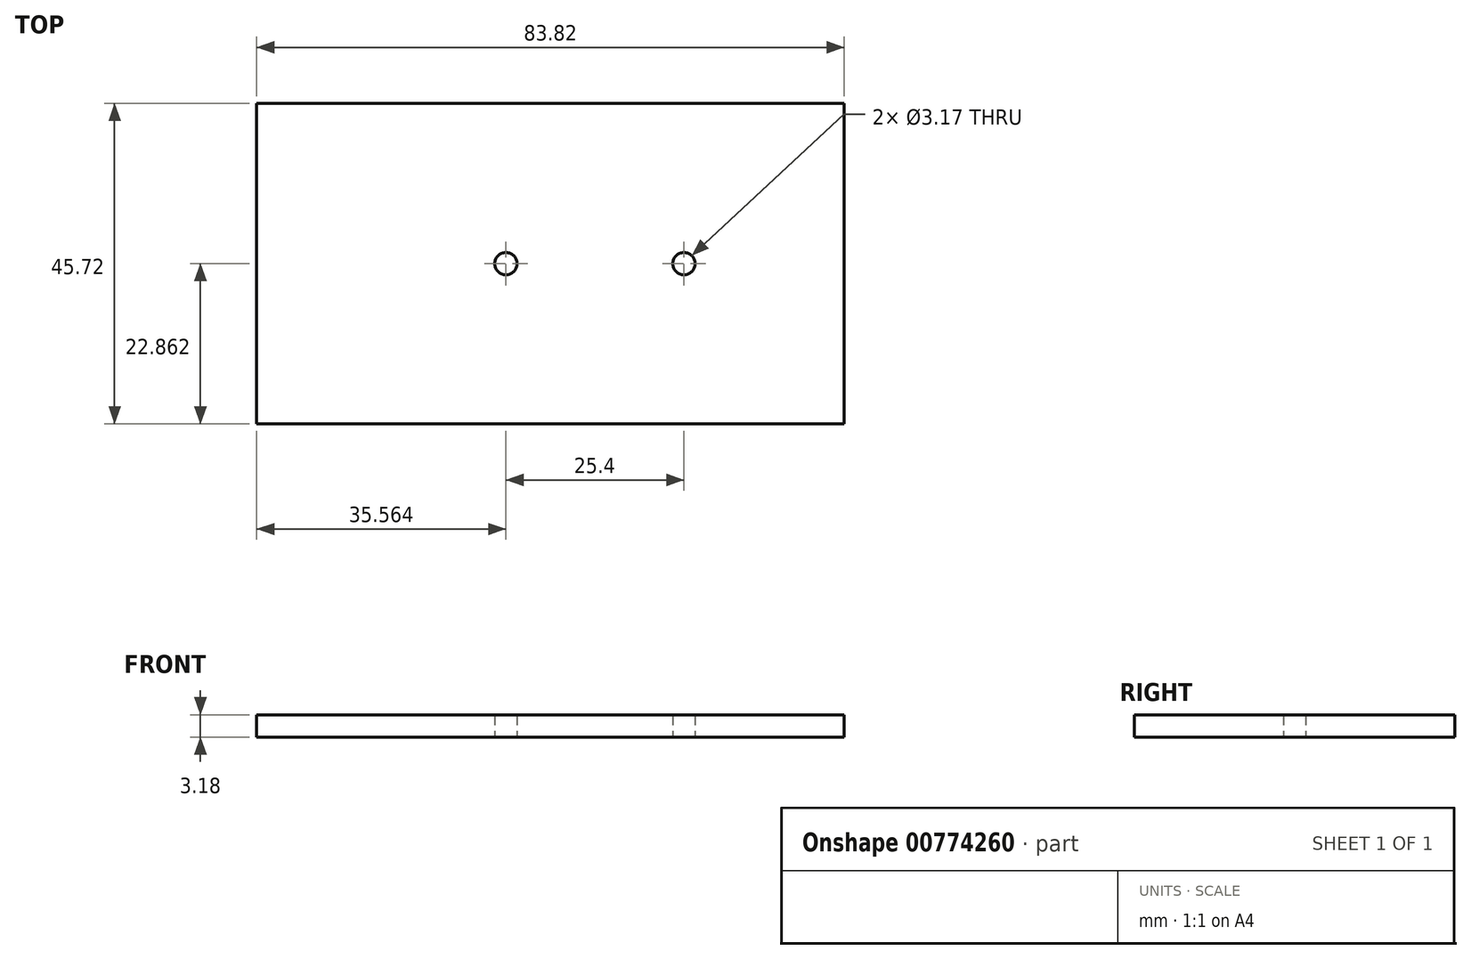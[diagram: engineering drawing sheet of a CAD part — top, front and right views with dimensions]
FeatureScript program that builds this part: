
annotation { "Feature Type Name" : "Feature", "Feature Type Description" : "" }
export const myFeature = defineFeature(function(context is Context, id is Id, definition is map)
    precondition{}
    {
        {
            var Q0;
            Q0=qCreatedBy(makeId("Top.planeOp"),FACE);
            var sketch = newSketch(context, id + "F0", { "sketchPlane" : qUnion([Q0])});
            skLineSegment(sketch, "E0.bottom", {"start": v(-37.94, 13.34) * mm, "end": v(45.88, 13.34) * mm});
            skLineSegment(sketch, "E0.top", {"start": v(-37.94, -32.38) * mm, "end": v(45.88, -32.38) * mm});
            skLineSegment(sketch, "E0.left", {"start": v(-37.94, 13.34) * mm, "end": v(-37.94, -32.38) * mm});
            skLineSegment(sketch, "E0.right", {"start": v(45.88, 13.34) * mm, "end": v(45.88, -32.38) * mm});
            skPoint(sketch, "E1", {"position": v(-2.38, -9.52) * mm});
            skPoint(sketch, "E2", {"position": v(23.02, -9.52) * mm});
            skCircle(sketch, "E3", {"center": v(-2.38, -9.52) * mm, "radius": 1.59 * mm});
            skCircle(sketch, "E4", {"center": v(23.02, -9.52) * mm, "radius": 1.59 * mm});
            skSolve(sketch);
        }
        {
            var Q0;
            Q0=makeQuery(id+"F0.imprint","IMPRINT",FACE,{"disambiguationData":[TD([[makeQuery(id+"F0.imprint","IMPRINT",EDGE,{"derivedFrom":sQuery(id+"F0.wireOp",EDGE,"E0.bottom")}),-1.0]])]});
            extrude(context, id + "F1", {"entities" : qUnion([Q0]), "depth" : 3.17 * mm, "offsetDistance" : 25.4 * mm});
        }
    });
